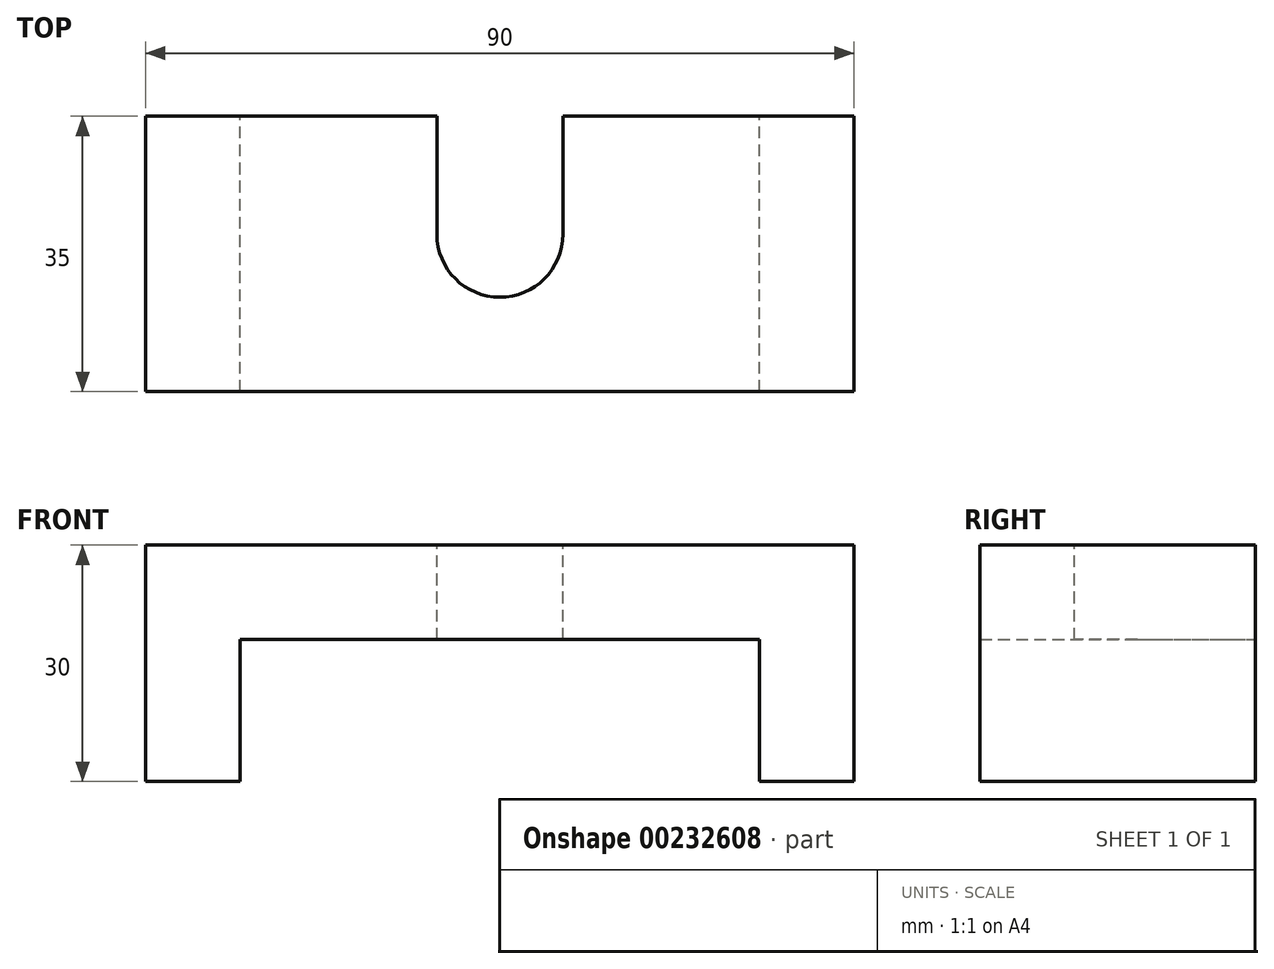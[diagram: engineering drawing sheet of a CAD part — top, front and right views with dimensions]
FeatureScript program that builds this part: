
annotation { "Feature Type Name" : "Feature", "Feature Type Description" : "" }
export const myFeature = defineFeature(function(context is Context, id is Id, definition is map)
    precondition{}
    {
        {
            var Q0;
            Q0=qCreatedBy(makeId("Front.planeOp"),FACE);
            var sketch = newSketch(context, id + "F0", { "sketchPlane" : qUnion([Q0])});
            skLineSegment(sketch, "E0", {"start": v(0, 0) * mm, "end": v(0, 30) * mm});
            skLineSegment(sketch, "E1", {"start": v(0, 30) * mm, "end": v(90, 30) * mm});
            skLineSegment(sketch, "E2", {"start": v(90, 30) * mm, "end": v(90, 0) * mm});
            skLineSegment(sketch, "E3", {"start": v(90, 0) * mm, "end": v(78, 0) * mm});
            skLineSegment(sketch, "E4", {"start": v(78, 0) * mm, "end": v(78, 18) * mm});
            skLineSegment(sketch, "E5", {"start": v(78, 18) * mm, "end": v(12, 18) * mm});
            skLineSegment(sketch, "E6", {"start": v(12, 18) * mm, "end": v(12, 0) * mm});
            skLineSegment(sketch, "E7", {"start": v(12, 0) * mm, "end": v(0, 0) * mm});
            skSolve(sketch);
        }
        {
            var Q0;
            Q0 = qSketchRegion(id + "F0", true);
            extrude(context, id + "F1", {"entities" : qUnion([Q0]), "depth" : 35 * mm});
        }
        {
            var Q0;
            Q0=makeQuery(id+"F1.opExtrude","SWEPT_FACE",FACE,{"disambiguationData":[OSD([sQuery(id+"F0.wireOp",EDGE,"E1")])]});
            var sketch = newSketch(context, id + "F2", { "sketchPlane" : qUnion([Q0])});
            skArc(sketch, "E8", {"start": v(37, -15) * mm, "mid": v(45, -23) * mm, "end": v(53, -15) * mm});
            skLineSegment(sketch, "E9", {"start": v(37, 0) * mm, "end": v(53, 0) * mm});
            skLineSegment(sketch, "E10", {"start": v(53, 0) * mm, "end": v(53, -15) * mm});
            skLineSegment(sketch, "E11", {"start": v(37, 0) * mm, "end": v(37, -15) * mm});
            skSolve(sketch);
        }
        {
            var Q0;
            Q0 = qSketchRegion(id + "F2", true);
            extrude(context, id + "F3", {"entities" : qUnion([Q0]), "operationType" : NewBodyOperationType.REMOVE, "endBound" : BoundingType.THROUGH_ALL, "oppositeDirection" : true, "depth" : 25 * mm});
        }
    });
